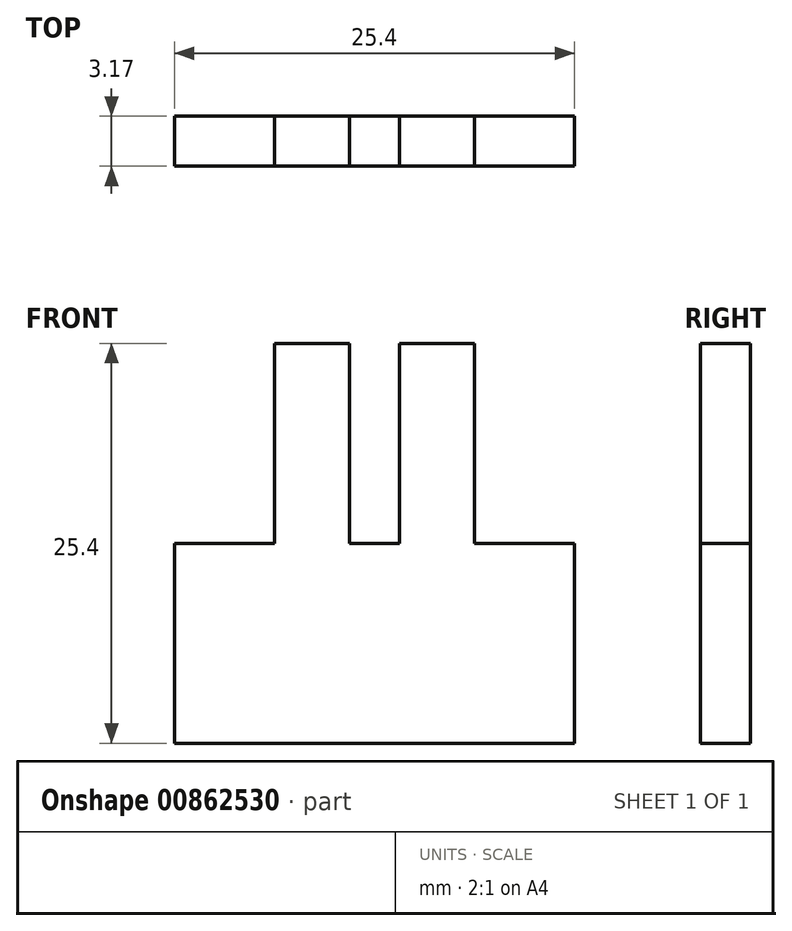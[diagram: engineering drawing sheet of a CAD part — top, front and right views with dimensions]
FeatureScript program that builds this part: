
annotation { "Feature Type Name" : "Feature", "Feature Type Description" : "" }
export const myFeature = defineFeature(function(context is Context, id is Id, definition is map)
    precondition{}
    {
        {
            var Q0;
            Q0=qCreatedBy(makeId("Front.planeOp"),FACE);
            var sketch = newSketch(context, id + "F0", { "sketchPlane" : qUnion([Q0])});
            skLineSegment(sketch, "E0", {"start": v(-12.7, 0) * mm, "end": v(0, 0) * mm, "construction": true});
            skLineSegment(sketch, "E1", {"start": v(0, 0) * mm, "end": v(-12.7, 0) * mm});
            skLineSegment(sketch, "E2", {"start": v(-12.7, 0) * mm, "end": v(-12.7, 12.7) * mm});
            skLineSegment(sketch, "E3", {"start": v(-12.7, 12.7) * mm, "end": v(-6.35, 12.7) * mm});
            skLineSegment(sketch, "E4", {"start": v(-6.35, 12.7) * mm, "end": v(-6.35, 25.4) * mm});
            skLineSegment(sketch, "E5", {"start": v(0, 0) * mm, "end": v(-1.59, 0) * mm, "construction": true});
            skLineSegment(sketch, "E6", {"start": v(-1.59, 25.4) * mm, "end": v(-1.59, 12.7) * mm});
            skLineSegment(sketch, "E7", {"start": v(-1.59, 12.7) * mm, "end": v(0, 12.7) * mm});
            skLineSegment(sketch, "E8", {"start": v(-6.35, 25.4) * mm, "end": v(-1.59, 25.4) * mm});
            skLineSegment(sketch, "E9.MirrorCS", {"start": v(0, 0) * mm, "end": v(1.59, 0) * mm, "construction": true});
            skLineSegment(sketch, "E10.MirrorCS", {"start": v(12.7, 0) * mm, "end": v(0, 0) * mm, "construction": true});
            skLineSegment(sketch, "E11.MirrorCS", {"start": v(1.59, 25.4) * mm, "end": v(1.59, 12.7) * mm});
            skLineSegment(sketch, "E12.MirrorCS", {"start": v(1.59, 12.7) * mm, "end": v(0, 12.7) * mm});
            skLineSegment(sketch, "E13.MirrorCS", {"start": v(6.35, 12.7) * mm, "end": v(6.35, 25.4) * mm});
            skLineSegment(sketch, "E14.MirrorCS", {"start": v(12.7, 0) * mm, "end": v(12.7, 12.7) * mm});
            skLineSegment(sketch, "E15.MirrorCS", {"start": v(12.7, 12.7) * mm, "end": v(6.35, 12.7) * mm});
            skLineSegment(sketch, "E16.MirrorCS", {"start": v(6.35, 25.4) * mm, "end": v(1.59, 25.4) * mm});
            skLineSegment(sketch, "E17.MirrorCS", {"start": v(0, 0) * mm, "end": v(12.7, 0) * mm});
            skSolve(sketch);
        }
        {
            var Q0;
            Q0 = qSketchRegion(id + "F0", true);
            extrude(context, id + "F1", {"entities" : qUnion([Q0]), "depth" : 3.17 * mm, "offsetDistance" : 25.4 * mm});
        }
    });
